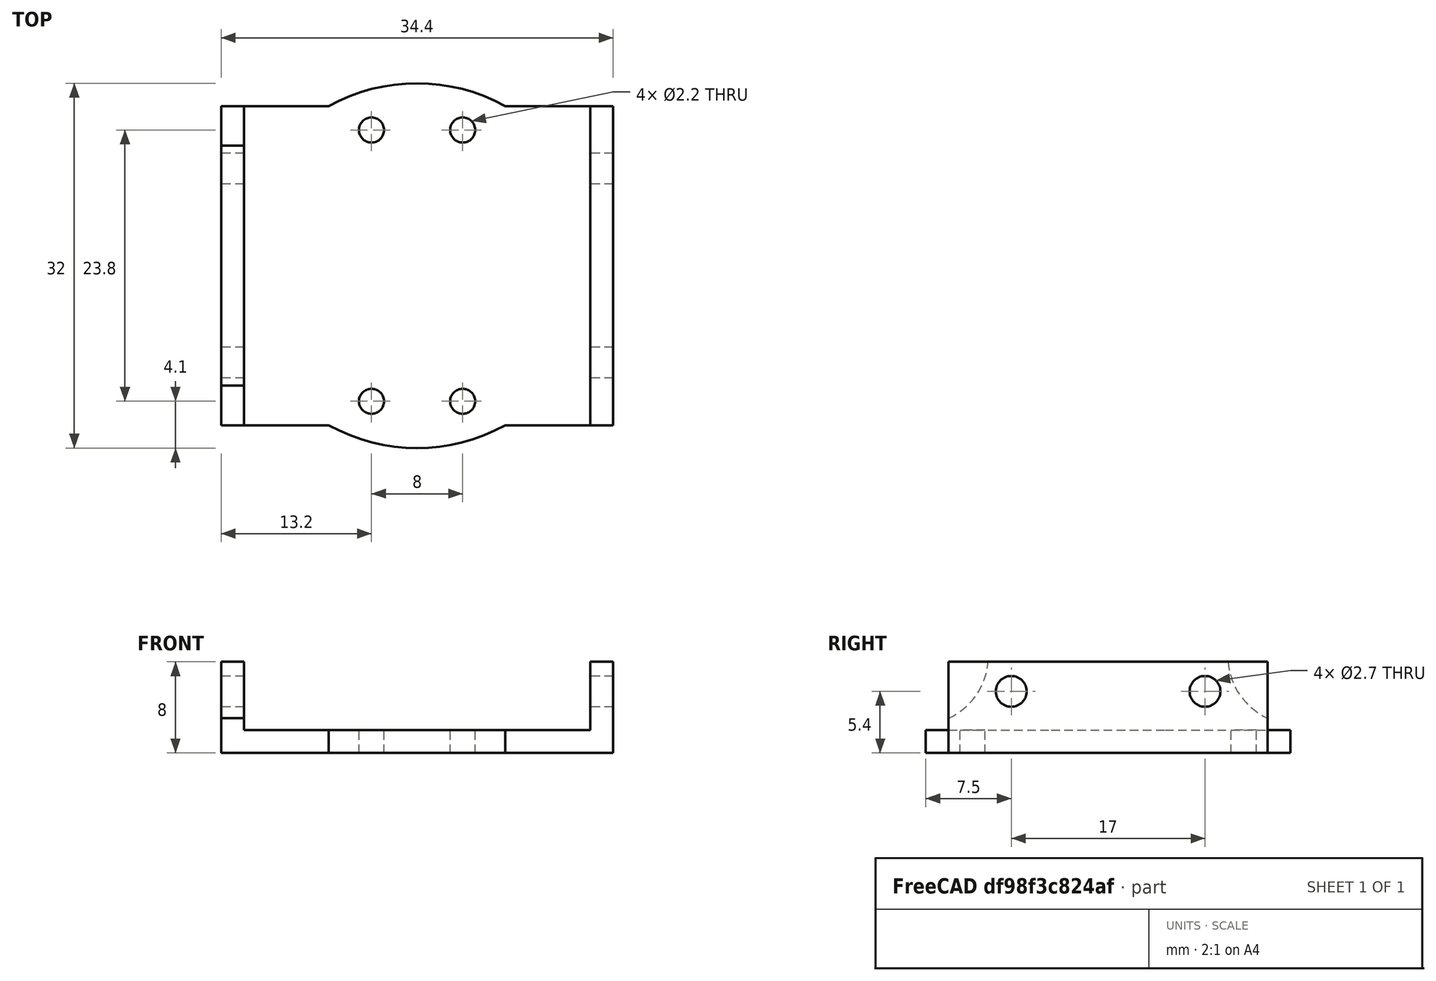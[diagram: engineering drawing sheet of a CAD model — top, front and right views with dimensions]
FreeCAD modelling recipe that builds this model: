
FCSTD DOCUMENT  (FreeCAD 0.15R4671 (Git))
Label: hub_plate
License: All rights reserved
LicenseURL: http://en.wikipedia.org/wiki/All_rights_reserved
objects: Part::Cylinder×9, Part::MultiFuse×5, Part::Box×3, Part::Cut×2
note: 19 computed .brp shape members not serialized (recipe doc carries the construction recipe); baked Part::Feature solids carry a one-line shape summary decoded from their .brp

FEATURE [Part::Box] Box  label="Cube"
  Height = 2
  Length = 30.4
  Width = 28
FEATURE [Part::Box] Box001  label="Cube001"
  Height = 8
  Length = 2
  Placement = pos=(-2,0,0) rot=(0,0,1;0rad)
  Width = 28
FEATURE [Part::Box] Box002  label="Cube002"
  Height = 8
  Length = 2
  Placement = pos=(30.4,0,0) rot=(0,0,1;0rad)
  Width = 28
FEATURE [Part::Cylinder] Cylinder
  Angle = 360
  Height = 100
  Placement = pos=(50,5.5,5.4) rot=(0,-1,0;1.5708rad)
  Radius = 1.35
FEATURE [Part::Cylinder] Cylinder001
  Angle = 360
  Height = 100
  Placement = pos=(50,22.5,5.4) rot=(0,-1,0;1.5708rad)
  Radius = 1.35
FEATURE [Part::Cylinder] Cylinder002
  Angle = 360
  Height = 100
  Placement = pos=(0,0,0) rot=(0,1,0;1.5708rad)
  Radius = 1.1
FEATURE [Part::Cylinder] Cylinder003
  Angle = 360
  Height = 100
  Placement = pos=(0,0,8) rot=(0,1,0;1.5708rad)
  Radius = 1.1
FEATURE [Part::Cylinder] Cylinder004
  Angle = 360
  Height = 100
  Placement = pos=(0,23.8,0) rot=(0,1,0;1.5708rad)
  Radius = 1.1
FEATURE [Part::Cylinder] Cylinder005
  Angle = 360
  Height = 100
  Placement = pos=(0,23.8,8) rot=(0,1,0;1.5708rad)
  Radius = 1.1
FEATURE [Part::MultiFuse] Fusion001
  Placement = pos=(19.2,2.1,0) rot=(0,-1,0;1.5708rad)
  Shapes = -> [Cylinder005,Cylinder002,Cylinder004,Cylinder003]
FEATURE [Part::Cylinder] Cylinder006
  Angle = 360
  Height = 2
  Placement = pos=(15.2,14,0) rot=(0,0,1;0rad)
  Radius = 16
FEATURE [Part::MultiFuse] Fusion
  Shapes = -> [Cylinder006,Box,Box001,Box002]
FEATURE [Part::MultiFuse] Fusion002
  Shapes = -> [Cylinder,Cylinder001]
FEATURE [Part::MultiFuse] Fusion003
  Shapes = -> [Fusion001,Fusion002]
FEATURE [Part::Cut] Cut
  Base = -> Fusion
  Tool = -> Fusion003
FEATURE [Part::Cylinder] Cylinder007
  Angle = 360
  Height = 15
  Placement = pos=(-10,-2.5,8.5) rot=(0,1,0;1.5708rad)
  Radius = 6
FEATURE [Part::Cylinder] Cylinder008
  Angle = 360
  Height = 15
  Placement = pos=(-10,30.5,8.5) rot=(0,1,0;1.5708rad)
  Radius = 6
FEATURE [Part::MultiFuse] Fusion004
  Shapes = -> [Cylinder008,Cylinder007]
FEATURE [Part::Cut] Cut001
  Base = -> Cut
  Tool = -> Fusion004
